# Revit family: Hager-Orion_Inox-IP55-D300-Cl.I-Inox_encl-630A-800mm-CH-de
name_source: partatom
category: Electrical Equipment
units: mm (PartAtom-declared; Revit-internal decimal feet)

## family parameters
Cut with Voids When Loaded = No
Host = Face
Panel Configuration = Two Columns, Circuits Across
Part Type = Panelboard
Room Calculation Point = No
Round Connector Dimension = Use Diameter
Shared = No

## types (4) — shared parameters
EF000003 - Montageart = EV000384 - Aufputz
EF000007 - Farbe = EV000154 - sonstige
EF000040 - Höhe = 800 mm  [stored 2.62467 ft]
EF000049 - Tiefe = 300 mm  [stored 0.984252 ft]
EF000118 - Mit Montageplatte = No
EF000339 - Art der Abdeckung = EV004216 - Tür
EF001088 - Anbaumöglichkeit = Yes
EF001131 - Innentiefe = 266 mm
EF001596 - Werkstoff des Gehäuses = EV000166 - rostfreier Stahl
EF001613 - Funktionserhalt = EV000494 - ohne
EF003532 - Geeignet für Außengebrauch = Yes
EF004293 - Schlagfestigkeit = EV008784 - IK10
EF004464 - Art der Tür = EV003602 - Doppel
EF005474 - Schutzart (IP) = EV006420 - IP55
EF006244 - Transparenter Deckel/Tür = No
EF006306 - Mit Schloss = Yes
EF007800 - Geeignet für Blitzschutz = No
EF008873 - Nennstrom (In) = 630 A
EF009170 - Materialstärke Gehäuse = 2 mm  [stored 0.00656168 ft]
EF009171 - Materialstärke Tür/Deckel = 2 mm  [stored 0.00656168 ft]
EF009212 - Ausführung Deckel = EV000116 - geschlossen
EF015940 - Deckel mit Überdruckentlastung = No
HG000002 - Mit tür = Yes
HG000003 - Bereich = Orion Inox
HG000006 - Unterputz = No
HG000009 - Doppelflügeligen Tür = No
HG000010 - Asymmetrische Türen = No
HG000023 - Gehäuse mit doppeltem Querschnitt = No
HG000024 - Höhe des unteren Teils = 800 mm  [stored 2.62467 ft]
HG000026 - Stehend auf dem Boden = No
Manufacturer = Hager
Type Comments = Orion Inox
zero-valued in all types: Default Elevation, EF000218 - Einbautiefe, EF000266 - Anzahl der Reihen, EF000437 - Anzahl der Leitungseinführungen, EF002950 - Breite in Teilungseinheiten, EF004427 - Anzahl der Module, EF009554 - Anzahl der Öffnungen für Flanschplatten, HG000027 - Sockelhöhe

## per-type parameters (varying)
| type | EF000008 - Breite | HG000004 - Herstellerreferenz |
| Aufputz IP55 B1000 H800 T300  - FL054BW | 1000 mm  [stored 3.28084 ft] | FL054BW |
| Aufputz IP55 B1000 H800 T300  - FL054BWL | 1000 mm  [stored 3.28084 ft] | FL054BWL |
| Aufputz IP55 B1200 H800 T300  - FL055BW | 1200 mm  [stored 3.93701 ft] | FL055BW |
| Aufputz IP55 B1200 H800 T300  - FL055BWL | 1200 mm  [stored 3.93701 ft] | FL055BWL |

note: [stored X ft] marks values corroborated as IEEE doubles in the binary element streams (Revit-internal decimal feet)

## geometry (parser evidence)
native form markers: Sweep x7
no freeform markers — native parametric forms only
